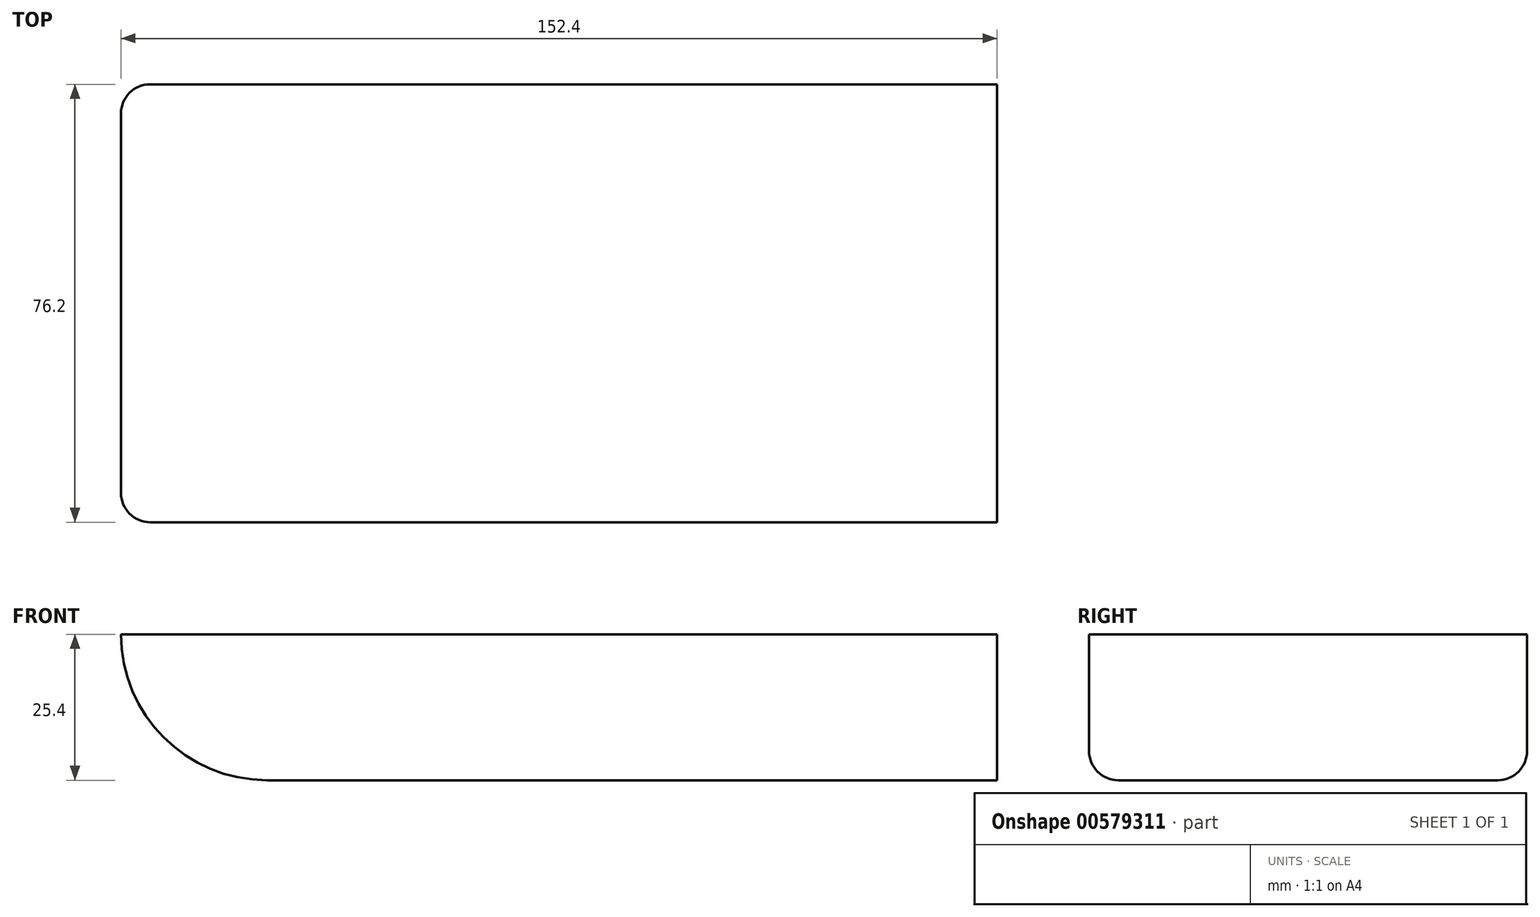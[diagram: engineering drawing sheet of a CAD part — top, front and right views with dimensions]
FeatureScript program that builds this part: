
annotation { "Feature Type Name" : "Feature", "Feature Type Description" : "" }
export const myFeature = defineFeature(function(context is Context, id is Id, definition is map)
    precondition{}
    {
        {
            var Q0;
            Q0=qCreatedBy(makeId("Front.planeOp"),FACE);
            var sketch = newSketch(context, id + "F0", { "sketchPlane" : qUnion([Q0])});
            skLineSegment(sketch, "E0.bottom", {"start": v(-53.35, 5.11) * mm, "end": v(73.65, 5.11) * mm});
            skLineSegment(sketch, "E0.top", {"start": v(-53.35, -20.29) * mm, "end": v(73.65, -20.29) * mm});
            skLineSegment(sketch, "E0.left", {"start": v(-53.35, 5.11) * mm, "end": v(-53.35, -20.29) * mm});
            skLineSegment(sketch, "E0.right", {"start": v(73.65, 5.11) * mm, "end": v(73.65, -20.29) * mm});
            skPoint(sketch, "E1.1.internal.snap0", {"position": v(-68, 11.1) * mm});
            skLineSegment(sketch, "E2", {"start": v(-53.35, 5.11) * mm, "end": v(-78.75, 5.11) * mm});
            skArc(sketch, "E3", {"start": v(-78.75, 5.11) * mm, "mid": v(-71.3, -12.85) * mm, "end": v(-53.35, -20.29) * mm});
            skSolve(sketch);
        }
        {
            var Q0;
            Q0=makeQuery(id+"F0.imprint","IMPRINT",FACE,{"disambiguationData":[TD([[makeQuery(id+"F0.imprint","IMPRINT",EDGE,{"derivedFrom":sQuery(id+"F0.wireOp",EDGE,"E0.left")}),-1.0]])]});
            var Q1;
            Q1=makeQuery(id+"F0.imprint","IMPRINT",FACE,{"disambiguationData":[TD([[makeQuery(id+"F0.imprint","IMPRINT",EDGE,{"derivedFrom":sQuery(id+"F0.wireOp",EDGE,"E0.bottom")}),-1.0]])]});
            extrude(context, id + "F1", {"entities" : qUnion([Q0, Q1]), "depth" : 76.2 * mm, "offsetDistance" : 25.4 * mm});
        }
        {
            var Q0;
            Q0=makeQuery(id+"F1.opExtrude","CAP_EDGE",EDGE,{"disambiguationData":[OSD([sQuery(id+"F0.wireOp",EDGE,"E3")])],"isStart":false});
            var Q1;
            Q1=makeQuery(id+"F1.opExtrude","CAP_EDGE",EDGE,{"disambiguationData":[OSD([sQuery(id+"F0.wireOp",EDGE,"E3")])],"isStart":true});
            fillet(context, id + "F2", {"entities" : qUnion([Q0, Q1]), "radius" : 5.08 * mm, "tangentPropagation" : true, "allowEdgeOverflow" : false});
        }
    });
